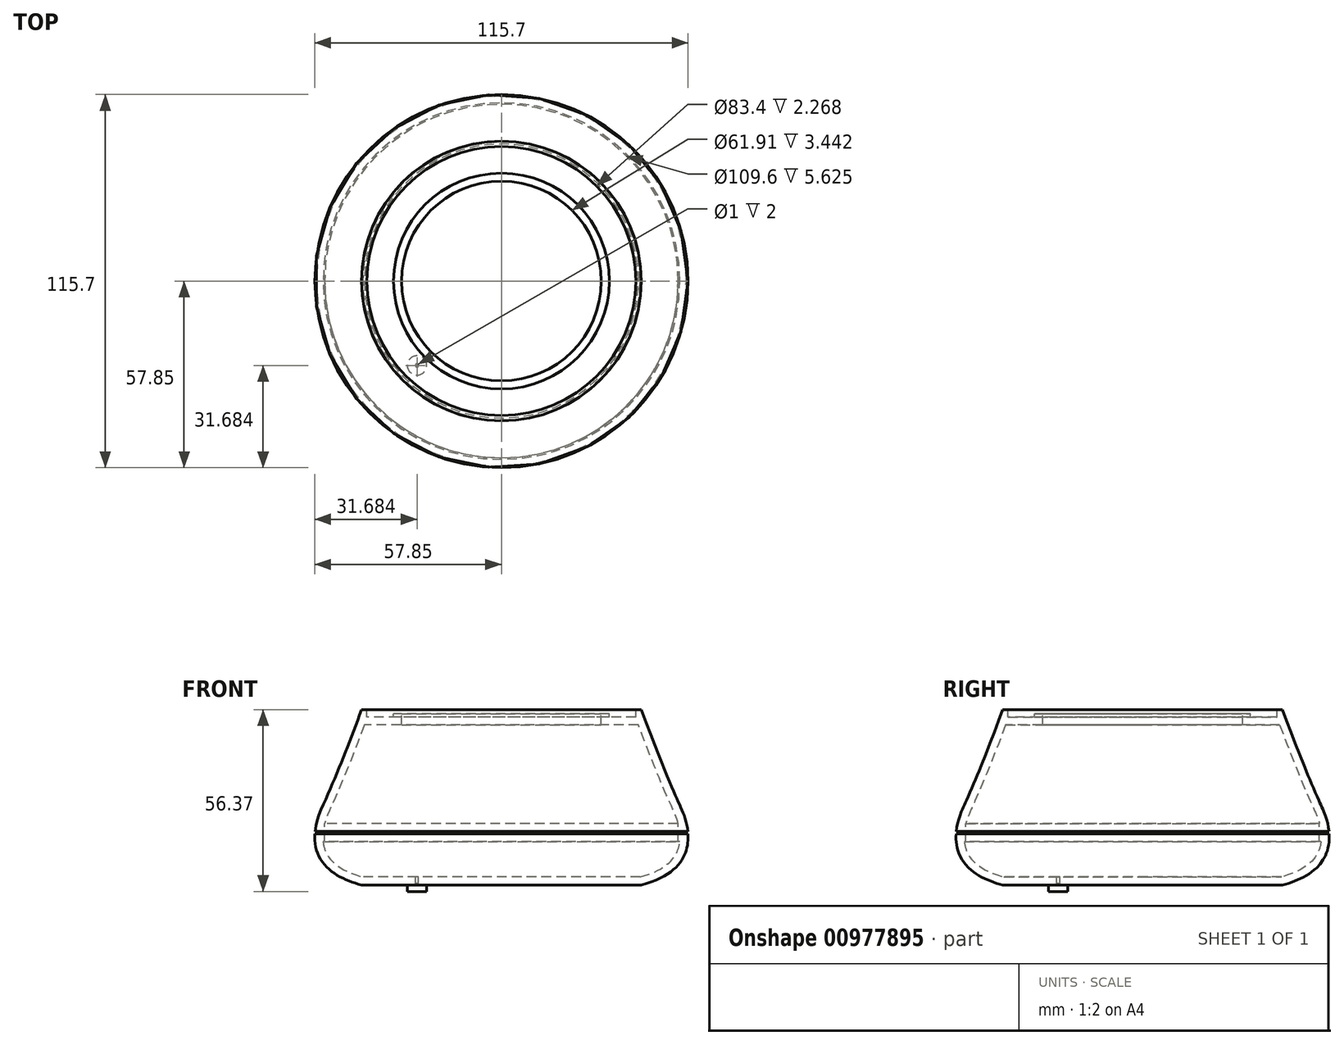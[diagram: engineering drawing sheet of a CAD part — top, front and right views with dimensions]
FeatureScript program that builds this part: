
annotation { "Feature Type Name" : "Feature", "Feature Type Description" : "" }
export const myFeature = defineFeature(function(context is Context, id is Id, definition is map)
    precondition{}
    {
        {
            var Q0;
            Q0=qCreatedBy(makeId("Front.planeOp"),FACE);
            var sketch = newSketch(context, id + "F0", { "sketchPlane" : qUnion([Q0])});
            skLineSegment(sketch, "E0", {"start": v(0, 0) * mm, "end": v(-43.35, 0) * mm});
            skLineSegment(sketch, "E1", {"start": v(-43.35, 54.37) * mm, "end": v(-41.7, 54.37) * mm});
            skLineSegment(sketch, "E2", {"start": v(0, 53.04) * mm, "end": v(0, 0) * mm});
            skFitSpline(sketch, "E3", {"points": [v(-43.35, 0) * mm, v(-57.85, 15.25) * mm, v(-56.07, 22.98) * mm, v(-43.35, 54.37) * mm], "startDerivative": vector(-109.43, 28.72) * mm, "endDerivative": vector(58.72, 157.64) * mm});
            skPoint(sketch, "E4", {"position": v(-57.83, 15.9) * mm});
            skPoint(sketch, "E5", {"position": v(-57.77, 16.6) * mm});
            skLineSegment(sketch, "E6", {"start": v(-57.83, 15.9) * mm, "end": v(-57.3, 15.9) * mm});
            skLineSegment(sketch, "E7", {"start": v(-57.3, 15.9) * mm, "end": v(-57.3, 16.6) * mm});
            skLineSegment(sketch, "E8", {"start": v(-57.3, 16.6) * mm, "end": v(-57.77, 16.6) * mm});
            skPoint(sketch, "E9", {"position": v(-41.7, 54.37) * mm});
            skPoint(sketch, "E10", {"position": v(-39.28, 54.37) * mm});
            skLineSegment(sketch, "E11", {"start": v(-41.7, 54.37) * mm, "end": v(-41.7, 52.1) * mm});
            skLineSegment(sketch, "E12", {"start": v(-41.7, 52.1) * mm, "end": v(-33.45, 52.1) * mm});
            skLineSegment(sketch, "E13", {"start": v(-33.45, 52.1) * mm, "end": v(-33.45, 53.04) * mm});
            skLineSegment(sketch, "E14", {"start": v(-33.45, 53.04) * mm, "end": v(0, 53.04) * mm});
            skPoint(sketch, "E15.orphan", {"position": v(0, 54.37) * mm});
            skSolve(sketch);
        }
        {
            var Q0;
            Q0=makeQuery(id+"F0.imprint","IMPRINT",FACE,{"disambiguationData":[TD([[makeQuery(id+"F0.imprint","IMPRINT",EDGE,{"derivedFrom":sQuery(id+"F0.wireOp",EDGE,"E0")}),-1.0]])]});
            var Q1;
            Q1=sQuery(id+"F0.wireOp",EDGE,"E2");
            revolve(context, id + "F1", {"surfaceOperationType" : NewSurfaceOperationType.NEW, "entities" : qUnion([Q0]), "axis" : qUnion([Q1]), "revolveType" : RevolveType.FULL});
        }
        {
            var Q0;
            Q0=makeQuery(id+"F1.opRevolve","SWEPT_FACE",FACE,{"disambiguationData":[OSD([sQuery(id+"F0.wireOp",EDGE,"E0")])]});
            var sketch = newSketch(context, id + "F2", { "sketchPlane" : qUnion([Q0])});
            skLineSegment(sketch, "E16", {"start": v(43.35, 0) * mm, "end": v(-43.35, 0) * mm});
            skLineSegment(sketch, "E17", {"start": v(0, 43.35) * mm, "end": v(-43.35, 0) * mm});
            skLineSegment(sketch, "E18", {"start": v(-21.68, 21.68) * mm, "end": v(30.65, -30.65) * mm});
            skLineSegment(sketch, "E19", {"start": v(-21.68, 21.68) * mm, "end": v(-30.65, 30.65) * mm});
            skCircle(sketch, "E20", {"center": v(-26.17, 26.17) * mm, "radius": 3 * mm});
            skSolve(sketch);
        }
        {
            var Q0;
            {var subQ0=sQuery(id+"F2.wireOp",EDGE,"E20");var subQ1=sQuery(id+"F2.wireOp",EDGE,"E19");var subQ2=makeQuery(id+"F2.imprint","INTERSECT",VERTEX,{"disambiguationData":[OD(0.0)],"derivedFrom":[subQ1,subQ0]});Q0=makeQuery(id+"F2.imprint","IMPRINT",FACE,{"disambiguationData":[TD([[makeQuery(id+"F2.imprint","IMPRINT",EDGE,{"disambiguationData":[TD([[subQ2,-1.0]])],"derivedFrom":subQ1}),1.0]])]});}
            var Q1;
            {var subQ0=sQuery(id+"F2.wireOp",EDGE,"E20");var subQ1=sQuery(id+"F2.wireOp",EDGE,"E19");var subQ2=makeQuery(id+"F2.imprint","INTERSECT",VERTEX,{"disambiguationData":[OD(0.0)],"derivedFrom":[subQ1,subQ0]});Q1=makeQuery(id+"F2.imprint","IMPRINT",FACE,{"disambiguationData":[TD([[makeQuery(id+"F2.imprint","IMPRINT",EDGE,{"disambiguationData":[TD([[subQ2,-1.0]])],"derivedFrom":subQ1}),-1.0]])]});}
            extrude(context, id + "F3", {"entities" : qUnion([Q0, Q1]), "operationType" : NewBodyOperationType.ADD, "depth" : 2 * mm, "offsetDistance" : 25 * mm});
        }
        {
            var Q0;
            Q0=makeQuery(id+"F1.opRevolve","SWEPT_FACE",FACE,{"disambiguationData":[OSD([sQuery(id+"F0.wireOp",EDGE,"E14")])]});
            shell(context, id + "F4", {"entities" : qUnion([Q0]), "thickness" : 2.5 * mm});
        }
    });
